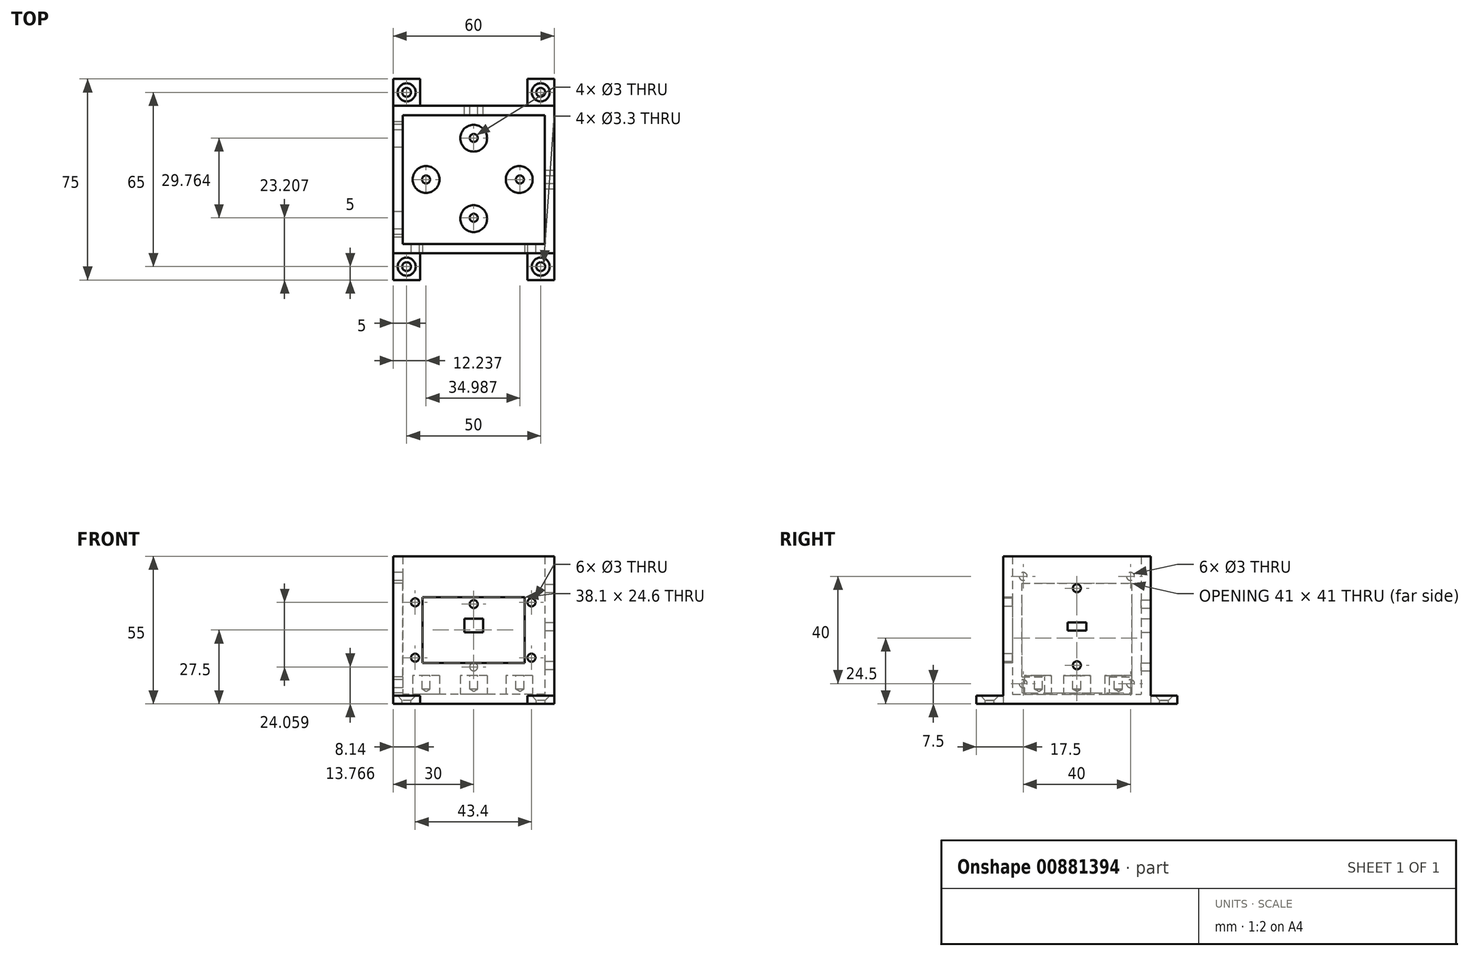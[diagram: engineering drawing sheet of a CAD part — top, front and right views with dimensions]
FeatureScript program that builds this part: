
annotation { "Feature Type Name" : "Feature", "Feature Type Description" : "" }
export const myFeature = defineFeature(function(context is Context, id is Id, definition is map)
    precondition{}
    {
        {
            var Q0;
            Q0=qCreatedBy(makeId("Top.planeOp"),FACE);
            var sketch = newSketch(context, id + "F0", { "sketchPlane" : qUnion([Q0])});
            skLineSegment(sketch, "E0.bottom", {"start": v(30, -27.5) * mm, "end": v(-30, -27.5) * mm});
            skLineSegment(sketch, "E0.top", {"start": v(30, 27.5) * mm, "end": v(-30, 27.5) * mm});
            skLineSegment(sketch, "E0.left", {"start": v(30, -27.5) * mm, "end": v(30, 27.5) * mm});
            skLineSegment(sketch, "E0.right", {"start": v(-30, -27.5) * mm, "end": v(-30, 27.5) * mm});
            skPoint(sketch, "E0.middle", {"position": v(0, 0) * mm});
            skSolve(sketch);
        }
        {
            var Q0;
            Q0=makeQuery(id+"F0.imprint","IMPRINT",FACE,{"disambiguationData":[TD([[makeQuery(id+"F0.imprint","IMPRINT",EDGE,{"derivedFrom":sQuery(id+"F0.wireOp",EDGE,"E0.bottom")}),-1.0]])]});
            extrude(context, id + "F1", {"entities" : qUnion([Q0]), "depth" : 55 * mm, "offsetDistance" : 25 * mm});
        }
        {
            var Q0;
            Q0=makeQuery(id+"F1.opExtrude","CAP_FACE",FACE,{"disambiguationData":[OSD([sQuery(id+"F0.wireOp",EDGE,"E0.bottom"),sQuery(id+"F0.wireOp",EDGE,"E0.top"),sQuery(id+"F0.wireOp",EDGE,"E0.left"),sQuery(id+"F0.wireOp",EDGE,"E0.right")])],"isStart":false});
            shell(context, id + "F2", {"entities" : qUnion([Q0]), "thickness" : 3.5 * mm});
        }
        {
            var Q0;
            Q0=makeQuery(id+"F1.opExtrude","SWEPT_FACE",FACE,{"disambiguationData":[OSD([sQuery(id+"F0.wireOp",EDGE,"E0.bottom")])]});
            var sketch = newSketch(context, id + "F3", { "sketchPlane" : qUnion([Q0])});
            skPoint(sketch, "E1", {"position": v(0, 27.5) * mm});
            skPoint(sketch, "E2", {"position": v(0, 39.8) * mm});
            skPoint(sketch, "E3", {"position": v(0, 15.2) * mm});
            skPoint(sketch, "E4", {"position": v(-19.05, 39.8) * mm});
            skPoint(sketch, "E5", {"position": v(19.05, 39.8) * mm});
            skPoint(sketch, "E6", {"position": v(-19.05, 15.2) * mm});
            skPoint(sketch, "E7", {"position": v(19.05, 15.2) * mm});
            skLineSegment(sketch, "E8", {"start": v(-19.05, 39.8) * mm, "end": v(-19.05, 15.2) * mm});
            skLineSegment(sketch, "E9", {"start": v(0, 15.2) * mm, "end": v(-19.05, 15.2) * mm});
            skLineSegment(sketch, "E10", {"start": v(0, 15.2) * mm, "end": v(19.05, 15.2) * mm});
            skLineSegment(sketch, "E11", {"start": v(19.05, 15.2) * mm, "end": v(19.05, 39.8) * mm});
            skLineSegment(sketch, "E12", {"start": v(-19.05, 39.8) * mm, "end": v(19.05, 39.8) * mm});
            skSolve(sketch);
        }
        {
            var Q0;
            Q0=makeQuery(id+"F3.imprint","IMPRINT",FACE,{"disambiguationData":[TD([[makeQuery(id+"F3.imprint","IMPRINT",EDGE,{"derivedFrom":sQuery(id+"F3.wireOp",EDGE,"E8")}),1.0]])]});
            extrude(context, id + "F4", {"entities" : qUnion([Q0]), "operationType" : NewBodyOperationType.REMOVE, "oppositeDirection" : true, "depth" : 5 * mm, "offsetDistance" : 25 * mm});
        }
        {
            var Q0;
            Q0=makeQuery(id+"F1.opExtrude","SWEPT_FACE",FACE,{"disambiguationData":[OSD([sQuery(id+"F0.wireOp",EDGE,"E0.bottom")])]});
            var sketch = newSketch(context, id + "F5", { "sketchPlane" : qUnion([Q0])});
            skPoint(sketch, "E13", {"position": v(21.54, 37.82) * mm});
            skPoint(sketch, "E14", {"position": v(21.54, 17.17) * mm});
            skPoint(sketch, "E15", {"position": v(-21.86, 17.17) * mm});
            skPoint(sketch, "E16", {"position": v(-21.86, 37.82) * mm});
            skPoint(sketch, "E17", {"position": v(19.05, 27.5) * mm});
            skPoint(sketch, "E18", {"position": v(21.54, 27.5) * mm});
            skSolve(sketch);
        }
        {
            var Q0;
            Q0=sQuery(id+"F5.wireOp",VERTEX,"E16");
            var Q1;
            Q1=sQuery(id+"F5.wireOp",VERTEX,"E15");
            var Q2;
            Q2=sQuery(id+"F5.wireOp",VERTEX,"E14");
            var Q3;
            Q3=sQuery(id+"F5.wireOp",VERTEX,"E13");
            var Q4;
            Q4=makeQuery(id+"F1.opExtrude","SWEPT_BODY",BODY,{"disambiguationData":[OSD([sQuery(id+"F0.wireOp",EDGE,"E0.bottom"),sQuery(id+"F0.wireOp",EDGE,"E0.top"),sQuery(id+"F0.wireOp",EDGE,"E0.left"),sQuery(id+"F0.wireOp",EDGE,"E0.right")])]});
            hole(context, id + "F6", {"style" : HoleStyle.SIMPLE, "endStyle" : HoleEndStyle.BLIND, "holeDiameter" : 3 * mm, "majorDiameter" : 5 * mm, "holeDepth" : 12 * mm, "isTappedThrough" : true, "tappedDepth" : 12 * mm, "tapClearance" : 3, "startFromSketch" : true, "locations" : qUnion([Q0, Q1, Q2, Q3]), "scope" : qUnion([Q4])});
        }
        {
            var Q0;
            Q0=makeQuery(id+"F1.opExtrude","SWEPT_FACE",FACE,{"disambiguationData":[OSD([sQuery(id+"F0.wireOp",EDGE,"E0.right")])]});
            var sketch = newSketch(context, id + "F7", { "sketchPlane" : qUnion([Q0])});
            skPoint(sketch, "E19", {"position": v(0, 27.5) * mm});
            skLineSegment(sketch, "E20.bottom", {"start": v(20.5, 10) * mm, "end": v(-20.5, 10) * mm});
            skLineSegment(sketch, "E20.top", {"start": v(20.5, 45) * mm, "end": v(-20.5, 45) * mm});
            skLineSegment(sketch, "E20.left", {"start": v(20.5, 10) * mm, "end": v(20.5, 45) * mm});
            skLineSegment(sketch, "E20.right", {"start": v(-20.5, 10) * mm, "end": v(-20.5, 45) * mm});
            skPoint(sketch, "E21", {"position": v(20, 27.5) * mm});
            skPoint(sketch, "E22", {"position": v(20, 47.5) * mm});
            skPoint(sketch, "E23", {"position": v(20, 7.5) * mm});
            skPoint(sketch, "E24", {"position": v(-20, 47.5) * mm});
            skPoint(sketch, "E25", {"position": v(-20, 7.5) * mm});
            skPoint(sketch, "E26", {"position": v(0, 7.5) * mm});
            skPoint(sketch, "E27", {"position": v(0, 47.5) * mm});
            skSolve(sketch);
        }
        {
            var Q0;
            Q0=sQuery(id+"F7.wireOp",VERTEX,"E24");
            var Q1;
            Q1=sQuery(id+"F7.wireOp",VERTEX,"E25");
            var Q2;
            Q2=sQuery(id+"F7.wireOp",VERTEX,"E23");
            var Q3;
            Q3=sQuery(id+"F7.wireOp",VERTEX,"E22");
            var Q4;
            Q4=makeQuery(id+"F1.opExtrude","SWEPT_BODY",BODY,{"disambiguationData":[OSD([sQuery(id+"F0.wireOp",EDGE,"E0.bottom"),sQuery(id+"F0.wireOp",EDGE,"E0.top"),sQuery(id+"F0.wireOp",EDGE,"E0.left"),sQuery(id+"F0.wireOp",EDGE,"E0.right")])]});
            hole(context, id + "F8", {"style" : HoleStyle.SIMPLE, "endStyle" : HoleEndStyle.BLIND, "holeDiameter" : 3 * mm, "majorDiameter" : 5 * mm, "holeDepth" : 12 * mm, "isTappedThrough" : true, "tappedDepth" : 12 * mm, "tapClearance" : 3, "startFromSketch" : true, "locations" : qUnion([Q0, Q1, Q2, Q3]), "scope" : qUnion([Q4])});
        }
        {
            var Q0;
            Q0=qSketchRegion(id+"F7",true);
            extrude(context, id + "F9", {"entities" : qUnion([Q0]), "operationType" : NewBodyOperationType.REMOVE, "oppositeDirection" : true, "depth" : 25 * mm, "offsetDistance" : 25 * mm});
        }
        {
            var Q0;
            Q0=makeQuery(id+"F2.opShell","OFFSET_FACE",FACE,{"disambiguationData":[OSD([sQuery(id+"F0.wireOp",EDGE,"E0.bottom"),sQuery(id+"F0.wireOp",EDGE,"E0.top"),sQuery(id+"F0.wireOp",EDGE,"E0.left"),sQuery(id+"F0.wireOp",EDGE,"E0.right")])]});
            var sketch = newSketch(context, id + "F10", { "sketchPlane" : qUnion([Q0])});
            skPoint(sketch, "E28", {"position": v(0, 15.4) * mm});
            skPoint(sketch, "E29", {"position": v(-17.76, 0) * mm});
            skPoint(sketch, "E30", {"position": v(16.97, 0) * mm});
            skPoint(sketch, "E31", {"position": v(0, -14.6) * mm});
            skCircle(sketch, "E32", {"center": v(0, 15.4) * mm, "radius": 5 * mm});
            skCircle(sketch, "E33", {"center": v(-17.76, 0) * mm, "radius": 5 * mm});
            skCircle(sketch, "E34", {"center": v(0, -14.6) * mm, "radius": 5 * mm});
            skCircle(sketch, "E35", {"center": v(16.97, 0) * mm, "radius": 5 * mm});
            skSolve(sketch);
        }
        {
            var Q0;
            Q0=makeQuery(id+"F10.imprint","IMPRINT",FACE,{"disambiguationData":[TD([[makeQuery(id+"F10.imprint","IMPRINT",EDGE,{"derivedFrom":sQuery(id+"F10.wireOp",EDGE,"E33")}),1.0]])]});
            var Q1;
            Q1=makeQuery(id+"F10.imprint","IMPRINT",FACE,{"disambiguationData":[TD([[makeQuery(id+"F10.imprint","IMPRINT",EDGE,{"derivedFrom":sQuery(id+"F10.wireOp",EDGE,"E32")}),1.0]])]});
            var Q2;
            Q2=makeQuery(id+"F10.imprint","IMPRINT",FACE,{"disambiguationData":[TD([[makeQuery(id+"F10.imprint","IMPRINT",EDGE,{"derivedFrom":sQuery(id+"F10.wireOp",EDGE,"E35")}),1.0]])]});
            var Q3;
            Q3=makeQuery(id+"F10.imprint","IMPRINT",FACE,{"disambiguationData":[TD([[makeQuery(id+"F10.imprint","IMPRINT",EDGE,{"derivedFrom":sQuery(id+"F10.wireOp",EDGE,"E34")}),1.0]])]});
            extrude(context, id + "F11", {"entities" : qUnion([Q0, Q1, Q2, Q3]), "operationType" : NewBodyOperationType.ADD, "depth" : 7 * mm, "offsetDistance" : 25 * mm});
        }
        {
            var Q0;
            Q0=makeQuery(id+"F11.opExtrude","CAP_FACE",FACE,{"disambiguationData":[OSD([sQuery(id+"F10.wireOp",EDGE,"E33")])],"isStart":false});
            var sketch = newSketch(context, id + "F12", { "sketchPlane" : qUnion([Q0])});
            skPoint(sketch, "E36", {"position": v(-17.76, 0) * mm});
            skPoint(sketch, "E37", {"position": v(0, 15.47) * mm});
            skPoint(sketch, "E38", {"position": v(17.22, 0) * mm});
            skPoint(sketch, "E39", {"position": v(0, -14.3) * mm});
            skSolve(sketch);
        }
        {
            var Q0;
            Q0=sQuery(id+"F12.wireOp",VERTEX,"E37");
            var Q1;
            Q1=sQuery(id+"F12.wireOp",VERTEX,"E36");
            var Q2;
            Q2=sQuery(id+"F12.wireOp",VERTEX,"E39");
            var Q3;
            Q3=sQuery(id+"F12.wireOp",VERTEX,"E38");
            var Q4;
            Q4=makeQuery(id+"F1.opExtrude","SWEPT_BODY",BODY,{"disambiguationData":[OSD([sQuery(id+"F0.wireOp",EDGE,"E0.bottom"),sQuery(id+"F0.wireOp",EDGE,"E0.top"),sQuery(id+"F0.wireOp",EDGE,"E0.left"),sQuery(id+"F0.wireOp",EDGE,"E0.right")])]});
            hole(context, id + "F13", {"style" : HoleStyle.SIMPLE, "endStyle" : HoleEndStyle.BLIND, "holeDiameter" : 3 * mm, "majorDiameter" : 5 * mm, "holeDepth" : 5 * mm, "isTappedThrough" : true, "tappedDepth" : 12 * mm, "tapClearance" : 3, "startFromSketch" : true, "locations" : qUnion([Q0, Q1, Q2, Q3]), "scope" : qUnion([Q4])});
        }
        {
            var Q0;
            Q0=makeQuery(id+"F1.opExtrude","SWEPT_FACE",FACE,{"disambiguationData":[OSD([sQuery(id+"F0.wireOp",EDGE,"E0.left")])]});
            var sketch = newSketch(context, id + "F14", { "sketchPlane" : qUnion([Q0])});
            skLineSegment(sketch, "E40.bottom", {"start": v(3.5, 27.31) * mm, "end": v(-3.5, 27.31) * mm});
            skLineSegment(sketch, "E40.top", {"start": v(3.5, 30.31) * mm, "end": v(-3.5, 30.31) * mm});
            skLineSegment(sketch, "E40.left", {"start": v(3.5, 27.31) * mm, "end": v(3.5, 30.31) * mm});
            skLineSegment(sketch, "E40.right", {"start": v(-3.5, 27.31) * mm, "end": v(-3.5, 30.31) * mm});
            skPoint(sketch, "E40.middle", {"position": v(0, 28.81) * mm});
            skPoint(sketch, "E41", {"position": v(0, 48.81) * mm});
            skPoint(sketch, "E42", {"position": v(15, 48.81) * mm});
            skPoint(sketch, "E43", {"position": v(-15, 48.81) * mm});
            skPoint(sketch, "E44", {"position": v(0, 8.81) * mm});
            skPoint(sketch, "E45", {"position": v(-15, 8.81) * mm});
            skPoint(sketch, "E46", {"position": v(15, 8.81) * mm});
            skCircle(sketch, "E47", {"center": v(-15, 48.81) * mm, "radius": 2 * mm});
            skCircle(sketch, "E48", {"center": v(15, 48.81) * mm, "radius": 2 * mm});
            skCircle(sketch, "E49", {"center": v(0, 48.81) * mm, "radius": 2 * mm});
            skCircle(sketch, "E50", {"center": v(-15, 8.81) * mm, "radius": 2 * mm});
            skCircle(sketch, "E51", {"center": v(0, 8.81) * mm, "radius": 2 * mm});
            skCircle(sketch, "E52", {"center": v(15, 8.81) * mm, "radius": 2 * mm});
            skSolve(sketch);
        }
        {
            var Q0;
            Q0=makeQuery(id+"F14.imprint","IMPRINT",FACE,{"disambiguationData":[TD([[makeQuery(id+"F14.imprint","IMPRINT",EDGE,{"derivedFrom":sQuery(id+"F14.wireOp",EDGE,"E40.bottom")}),-1.0]])]});
            extrude(context, id + "F15", {"entities" : qUnion([Q0]), "operationType" : NewBodyOperationType.REMOVE, "oppositeDirection" : true, "depth" : 5 * mm, "offsetDistance" : 25 * mm});
        }
        {
            var Q0;
            Q0=makeQuery(id+"F1.opExtrude","SWEPT_FACE",FACE,{"disambiguationData":[OSD([sQuery(id+"F0.wireOp",EDGE,"E0.top")])]});
            var sketch = newSketch(context, id + "F16", { "sketchPlane" : qUnion([Q0])});
            skLineSegment(sketch, "E53.bottom", {"start": v(3.5, 26.7) * mm, "end": v(-3.5, 26.7) * mm});
            skLineSegment(sketch, "E53.top", {"start": v(3.5, 31.7) * mm, "end": v(-3.5, 31.7) * mm});
            skLineSegment(sketch, "E53.left", {"start": v(3.5, 26.7) * mm, "end": v(3.5, 31.7) * mm});
            skLineSegment(sketch, "E53.right", {"start": v(-3.5, 26.7) * mm, "end": v(-3.5, 31.7) * mm});
            skPoint(sketch, "E53.middle", {"position": v(0, 29.2) * mm});
            skSolve(sketch);
        }
        {
            var Q0;
            Q0=makeQuery(id+"F16.imprint","IMPRINT",FACE,{"disambiguationData":[TD([[makeQuery(id+"F16.imprint","IMPRINT",EDGE,{"derivedFrom":sQuery(id+"F16.wireOp",EDGE,"E53.bottom")}),-1.0]])]});
            extrude(context, id + "F17", {"entities" : qUnion([Q0]), "operationType" : NewBodyOperationType.REMOVE, "oppositeDirection" : true, "depth" : 5 * mm, "offsetDistance" : 25 * mm});
        }
        {
            var Q0;
            Q0=makeQuery(id+"F1.opExtrude","SWEPT_FACE",FACE,{"disambiguationData":[OSD([sQuery(id+"F0.wireOp",EDGE,"E0.right")])]});
            var sketch = newSketch(context, id + "F18", { "sketchPlane" : qUnion([Q0])});
            skPoint(sketch, "E54", {"position": v(0, 10) * mm});
            skPoint(sketch, "E55", {"position": v(12, 10) * mm});
            skPoint(sketch, "E56", {"position": v(-12, 10) * mm});
            skPoint(sketch, "E57", {"position": v(-12, 4) * mm});
            skPoint(sketch, "E58", {"position": v(12, 4) * mm});
            skLineSegment(sketch, "E59", {"start": v(-12, 10) * mm, "end": v(-12, 4) * mm});
            skLineSegment(sketch, "E60", {"start": v(12, 4) * mm, "end": v(-12, 4) * mm});
            skLineSegment(sketch, "E61", {"start": v(12, 4) * mm, "end": v(12, 10) * mm});
            skSolve(sketch);
        }
        {
            var Q0;
            {var subQ0=sQuery(id+"F18.wireOp",EDGE,"E59");Q0=makeQuery(id+"F18.imprint","IMPRINT",FACE,{"disambiguationData":[TD([[makeQuery(id+"F18.imprint","IMPRINT",EDGE,{"derivedFrom":subQ0}),1.0]])]});}
            extrude(context, id + "F19", {"entities" : qUnion([Q0]), "operationType" : NewBodyOperationType.REMOVE, "oppositeDirection" : true, "depth" : 4 * mm, "offsetDistance" : 25 * mm});
        }
        {
            var Q0;
            Q0=makeQuery(id+"F1.opExtrude","SWEPT_FACE",FACE,{"disambiguationData":[OSD([sQuery(id+"F0.wireOp",EDGE,"E0.left")])]});
            var sketch = newSketch(context, id + "F20", { "sketchPlane" : qUnion([Q0])});
            skPoint(sketch, "E62", {"position": v(0, 43.08) * mm});
            skPoint(sketch, "E63", {"position": v(0, 14.36) * mm});
            skSolve(sketch);
        }
        {
            var Q0;
            Q0=sQuery(id+"F20.wireOp",VERTEX,"E62");
            var Q1;
            Q1=sQuery(id+"F20.wireOp",VERTEX,"E63");
            var Q2;
            Q2=makeQuery(id+"F1.opExtrude","SWEPT_BODY",BODY,{"disambiguationData":[OSD([sQuery(id+"F0.wireOp",EDGE,"E0.bottom"),sQuery(id+"F0.wireOp",EDGE,"E0.top"),sQuery(id+"F0.wireOp",EDGE,"E0.left"),sQuery(id+"F0.wireOp",EDGE,"E0.right")])]});
            hole(context, id + "F21", {"style" : HoleStyle.SIMPLE, "endStyle" : HoleEndStyle.BLIND, "holeDiameter" : 3 * mm, "majorDiameter" : 5 * mm, "holeDepth" : 5 * mm, "isTappedThrough" : true, "tappedDepth" : 12 * mm, "tapClearance" : 3, "startFromSketch" : true, "locations" : qUnion([Q0, Q1]), "scope" : qUnion([Q2])});
        }
        {
            var Q0;
            Q0=makeQuery(id+"F1.opExtrude","SWEPT_FACE",FACE,{"disambiguationData":[OSD([sQuery(id+"F0.wireOp",EDGE,"E0.top")])]});
            var sketch = newSketch(context, id + "F22", { "sketchPlane" : qUnion([Q0])});
            skPoint(sketch, "E64", {"position": v(0, 37.18) * mm});
            skPoint(sketch, "E65", {"position": v(0, 13.77) * mm});
            skPoint(sketch, "E66", {"position": v(20, 3) * mm});
            skPoint(sketch, "E67", {"position": v(-20, 3) * mm});
            skLineSegment(sketch, "E68", {"start": v(-20, 3) * mm, "end": v(-30, 3) * mm});
            skLineSegment(sketch, "E69", {"start": v(-30, 3) * mm, "end": v(-20, 3) * mm});
            skLineSegment(sketch, "E70", {"start": v(-20, 0) * mm, "end": v(-20, 3) * mm});
            skLineSegment(sketch, "E71", {"start": v(20, 3) * mm, "end": v(20, 0) * mm});
            skLineSegment(sketch, "E72", {"start": v(20, 3) * mm, "end": v(30, 3) * mm});
            skSolve(sketch);
        }
        {
            var Q0;
            Q0=sQuery(id+"F22.wireOp",VERTEX,"E64");
            var Q1;
            Q1=sQuery(id+"F22.wireOp",VERTEX,"E65");
            var Q2;
            Q2=makeQuery(id+"F1.opExtrude","SWEPT_BODY",BODY,{"disambiguationData":[OSD([sQuery(id+"F0.wireOp",EDGE,"E0.bottom"),sQuery(id+"F0.wireOp",EDGE,"E0.top"),sQuery(id+"F0.wireOp",EDGE,"E0.left"),sQuery(id+"F0.wireOp",EDGE,"E0.right")])]});
            hole(context, id + "F23", {"style" : HoleStyle.SIMPLE, "endStyle" : HoleEndStyle.BLIND, "holeDiameter" : 3 * mm, "majorDiameter" : 5 * mm, "holeDepth" : 5 * mm, "isTappedThrough" : true, "tappedDepth" : 12 * mm, "tapClearance" : 3, "startFromSketch" : true, "locations" : qUnion([Q0, Q1]), "scope" : qUnion([Q2])});
        }
        {
            var Q0;
            Q0=makeQuery(id+"F1.opExtrude","SWEPT_FACE",FACE,{"disambiguationData":[OSD([sQuery(id+"F0.wireOp",EDGE,"E0.top")])]});
            var sketch = newSketch(context, id + "F24", { "sketchPlane" : qUnion([Q0])});
            skPoint(sketch, "E73", {"position": v(20, 3) * mm});
            skPoint(sketch, "E74", {"position": v(-20, 3) * mm});
            skLineSegment(sketch, "E75", {"start": v(-20, 3) * mm, "end": v(-30, 3) * mm});
            skLineSegment(sketch, "E76", {"start": v(-20, 3) * mm, "end": v(-20, 0) * mm});
            skLineSegment(sketch, "E77", {"start": v(20, 3) * mm, "end": v(20, 0) * mm});
            skLineSegment(sketch, "E78", {"start": v(20, 3) * mm, "end": v(30, 3) * mm});
            skSolve(sketch);
        }
        {
            var Q0;
            {var subQ0=sQuery(id+"F24.wireOp",EDGE,"E75");Q0=makeQuery(id+"F24.imprint","IMPRINT",FACE,{"disambiguationData":[TD([[makeQuery(id+"F24.imprint","IMPRINT",EDGE,{"derivedFrom":subQ0}),1.0]])]});}
            var Q1;
            {var subQ0=sQuery(id+"F24.wireOp",EDGE,"E77");Q1=makeQuery(id+"F24.imprint","IMPRINT",FACE,{"disambiguationData":[TD([[makeQuery(id+"F24.imprint","IMPRINT",EDGE,{"derivedFrom":subQ0}),1.0]])]});}
            extrude(context, id + "F25", {"entities" : qUnion([Q0, Q1]), "operationType" : NewBodyOperationType.ADD, "depth" : 10 * mm, "offsetDistance" : 25 * mm});
        }
        {
            var Q0;
            Q0=makeQuery(id+"F25.opExtrude","SWEPT_FACE",FACE,{"disambiguationData":[OSD([sQuery(id+"F24.wireOp",EDGE,"E75")])]});
            var sketch = newSketch(context, id + "F26", { "sketchPlane" : qUnion([Q0])});
            skPoint(sketch, "E79", {"position": v(25, 32.5) * mm});
            skSolve(sketch);
        }
        {
            var Q0;
            Q0=sQuery(id+"F26.wireOp",VERTEX,"E79");
            var Q1;
            Q1=makeQuery(id+"F1.opExtrude","SWEPT_BODY",BODY,{"disambiguationData":[OSD([sQuery(id+"F0.wireOp",EDGE,"E0.bottom"),sQuery(id+"F0.wireOp",EDGE,"E0.top"),sQuery(id+"F0.wireOp",EDGE,"E0.left"),sQuery(id+"F0.wireOp",EDGE,"E0.right")])]});
            hole(context, id + "F27", {"style" : HoleStyle.C_SINK, "endStyle" : HoleEndStyle.BLIND, "standardTappedOrClearance" : lookupTablePath({ "standard" : "ISO", "fit" : "Normal", "size" : "M3", "type" : "Clearance" }), "standardBlindInLast" : lookupTablePath({ "fit" : "Standard", "standard" : "ISO", "size" : "M3", "type" : "Clearance" }), "holeDiameter" : 3.3 * mm, "cSinkDiameter" : 6.72 * mm, "cSinkAngle" : 90 * degree, "majorDiameter" : 5 * mm, "holeDepth" : 5 * mm, "isTappedThrough" : true, "tappedDepth" : 12 * mm, "tapClearance" : 3, "startFromSketch" : true, "locations" : qUnion([Q0]), "scope" : qUnion([Q1])});
        }
        {
            var Q0;
            Q0=makeQuery(id+"F25.opExtrude","SWEPT_FACE",FACE,{"disambiguationData":[OSD([sQuery(id+"F24.wireOp",EDGE,"E78")])]});
            var sketch = newSketch(context, id + "F28", { "sketchPlane" : qUnion([Q0])});
            skPoint(sketch, "E80", {"position": v(-25, 32.5) * mm});
            skSolve(sketch);
        }
        {
            var Q0;
            Q0=sQuery(id+"F28.wireOp",VERTEX,"E80");
            var Q1;
            Q1=makeQuery(id+"F1.opExtrude","SWEPT_BODY",BODY,{"disambiguationData":[OSD([sQuery(id+"F0.wireOp",EDGE,"E0.bottom"),sQuery(id+"F0.wireOp",EDGE,"E0.top"),sQuery(id+"F0.wireOp",EDGE,"E0.left"),sQuery(id+"F0.wireOp",EDGE,"E0.right")])]});
            hole(context, id + "F29", {"style" : HoleStyle.C_SINK, "endStyle" : HoleEndStyle.BLIND, "standardTappedOrClearance" : lookupTablePath({ "standard" : "ISO", "fit" : "Normal", "size" : "M3", "type" : "Clearance" }), "standardBlindInLast" : lookupTablePath({ "fit" : "Standard", "standard" : "ISO", "size" : "M3", "type" : "Clearance" }), "holeDiameter" : 3.3 * mm, "cSinkDiameter" : 6.72 * mm, "cSinkAngle" : 90 * degree, "majorDiameter" : 5 * mm, "holeDepth" : 5 * mm, "isTappedThrough" : true, "tappedDepth" : 12 * mm, "tapClearance" : 3, "startFromSketch" : true, "locations" : qUnion([Q0]), "scope" : qUnion([Q1])});
        }
        {
            var Q0;
            Q0=makeQuery(id+"F1.opExtrude","SWEPT_FACE",FACE,{"disambiguationData":[OSD([sQuery(id+"F0.wireOp",EDGE,"E0.bottom")])]});
            var sketch = newSketch(context, id + "F30", { "sketchPlane" : qUnion([Q0])});
            skPoint(sketch, "E81", {"position": v(20, 3) * mm});
            skPoint(sketch, "E82", {"position": v(-20, 3) * mm});
            skLineSegment(sketch, "E83", {"start": v(-20, 3) * mm, "end": v(-30, 3) * mm});
            skLineSegment(sketch, "E84", {"start": v(-20, 3) * mm, "end": v(-20, 0) * mm});
            skLineSegment(sketch, "E85", {"start": v(20, 3) * mm, "end": v(20, 0) * mm});
            skLineSegment(sketch, "E86", {"start": v(20, 3) * mm, "end": v(30, 3) * mm});
            skSolve(sketch);
        }
        {
            var Q0;
            {var subQ0=sQuery(id+"F30.wireOp",EDGE,"E83");Q0=makeQuery(id+"F30.imprint","IMPRINT",FACE,{"disambiguationData":[TD([[makeQuery(id+"F30.imprint","IMPRINT",EDGE,{"derivedFrom":subQ0}),1.0]])]});}
            extrude(context, id + "F31", {"entities" : qUnion([Q0]), "operationType" : NewBodyOperationType.ADD, "depth" : 10 * mm, "offsetDistance" : 25 * mm});
        }
        {
            var Q0;
            {var subQ0=sQuery(id+"F30.wireOp",EDGE,"E85");Q0=makeQuery(id+"F30.imprint","IMPRINT",FACE,{"disambiguationData":[TD([[makeQuery(id+"F30.imprint","IMPRINT",EDGE,{"derivedFrom":subQ0}),1.0]])]});}
            extrude(context, id + "F32", {"entities" : qUnion([Q0]), "operationType" : NewBodyOperationType.ADD, "depth" : 10 * mm, "offsetDistance" : 25 * mm});
        }
        {
            var Q0;
            Q0=makeQuery(id+"F31.opExtrude","SWEPT_FACE",FACE,{"disambiguationData":[OSD([sQuery(id+"F30.wireOp",EDGE,"E83")])]});
            var sketch = newSketch(context, id + "F33", { "sketchPlane" : qUnion([Q0])});
            skPoint(sketch, "E87", {"position": v(-25, -32.5) * mm});
            skPoint(sketch, "E88", {"position": v(25, -32.5) * mm});
            skSolve(sketch);
        }
        {
            var Q0;
            Q0=sQuery(id+"F33.wireOp",VERTEX,"E87");
            var Q1;
            Q1=sQuery(id+"F33.wireOp",VERTEX,"E88");
            var Q2;
            Q2=makeQuery(id+"F1.opExtrude","SWEPT_BODY",BODY,{"disambiguationData":[OSD([sQuery(id+"F0.wireOp",EDGE,"E0.bottom"),sQuery(id+"F0.wireOp",EDGE,"E0.top"),sQuery(id+"F0.wireOp",EDGE,"E0.left"),sQuery(id+"F0.wireOp",EDGE,"E0.right")])]});
            hole(context, id + "F34", {"style" : HoleStyle.C_SINK, "endStyle" : HoleEndStyle.BLIND, "standardTappedOrClearance" : lookupTablePath({ "standard" : "ISO", "fit" : "Normal", "size" : "M3", "type" : "Clearance" }), "standardBlindInLast" : lookupTablePath({ "fit" : "Standard", "standard" : "ISO", "size" : "M3", "type" : "Clearance" }), "holeDiameter" : 3.3 * mm, "cSinkDiameter" : 6.72 * mm, "cSinkAngle" : 90 * degree, "majorDiameter" : 5 * mm, "holeDepth" : 5 * mm, "isTappedThrough" : true, "tappedDepth" : 12 * mm, "tapClearance" : 3, "startFromSketch" : true, "locations" : qUnion([Q0, Q1]), "scope" : qUnion([Q2])});
        }
    });
